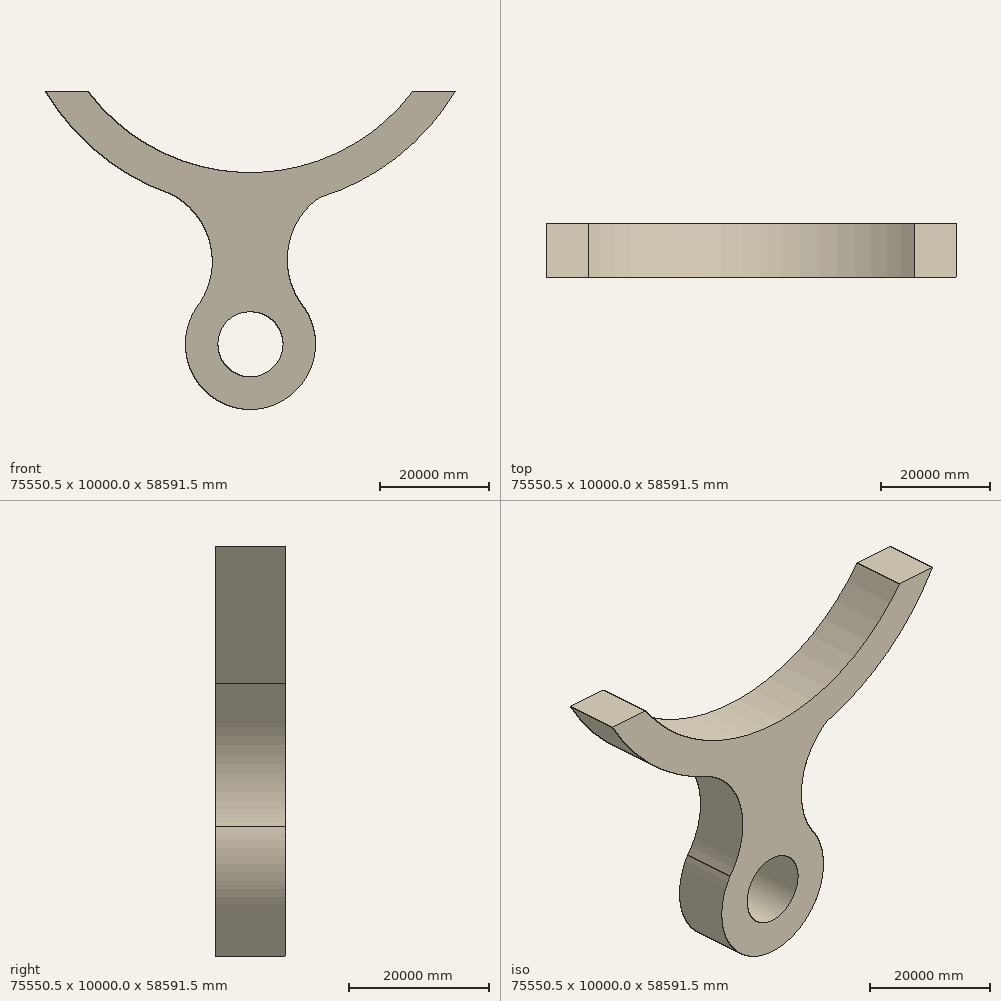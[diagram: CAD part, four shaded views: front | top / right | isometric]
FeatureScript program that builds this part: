
annotation { "Feature Type Name" : "Feature", "Feature Type Description" : "" }
export const myFeature = defineFeature(function(context is Context, id is Id, definition is map)
    precondition{}
    {
        {
            var Q0;
            Q0=qCreatedBy(makeId("Front.planeOp"),FACE);
            var sketch = newSketch(context, id + "F0", { "sketchPlane" : qUnion([Q0])});
            skArc(sketch, "E0", {"start": v(12791.35, -42099.66) * mm, "mid": v(27104.95, -34660.1) * mm, "end": v(37775.25, -22561.7) * mm});
            skArc(sketch, "E1", {"start": v(-29953.62, -22561.7) * mm, "mid": v(0, -37500) * mm, "end": v(29953.62, -22561.7) * mm});
            skArc(sketch, "E2", {"start": v(12791.35, -42099.66) * mm, "mid": v(6910.28, -51709.4) * mm, "end": v(10013.33, -62540.14) * mm});
            skArc(sketch, "E3", {"start": v(-10013.33, -62540.14) * mm, "mid": v(0, -81153.24) * mm, "end": v(10013.33, -62540.14) * mm});
            skArc(sketch, "E4", {"start": v(-10013.33, -62540.14) * mm, "mid": v(-7344.02, -51011.02) * mm, "end": v(-14460.61, -41555.87) * mm});
            skCircle(sketch, "E5", {"center": v(0, -69153.24) * mm, "radius": 6000 * mm});
            skLineSegment(sketch, "E6", {"start": v(-37775.25, -22561.7) * mm, "end": v(-29953.62, -22561.7) * mm});
            skArc(sketch, "E7.trimOffspring", {"start": v(-37775.25, -22561.7) * mm, "mid": v(-27791.02, -34112.45) * mm, "end": v(-14460.61, -41555.87) * mm});
            skLineSegment(sketch, "E8.trimOffspring", {"start": v(29953.62, -22561.7) * mm, "end": v(37775.25, -22561.7) * mm});
            skSolve(sketch);
        }
        {
            var Q0;
            Q0 = qSketchRegion(id + "F0", true);
            extrude(context, id + "F1", {"entities" : qUnion([Q0]), "oppositeDirection" : true, "depth" : 10000 * mm, "offsetDistance" : 25 * mm});
        }
    });
